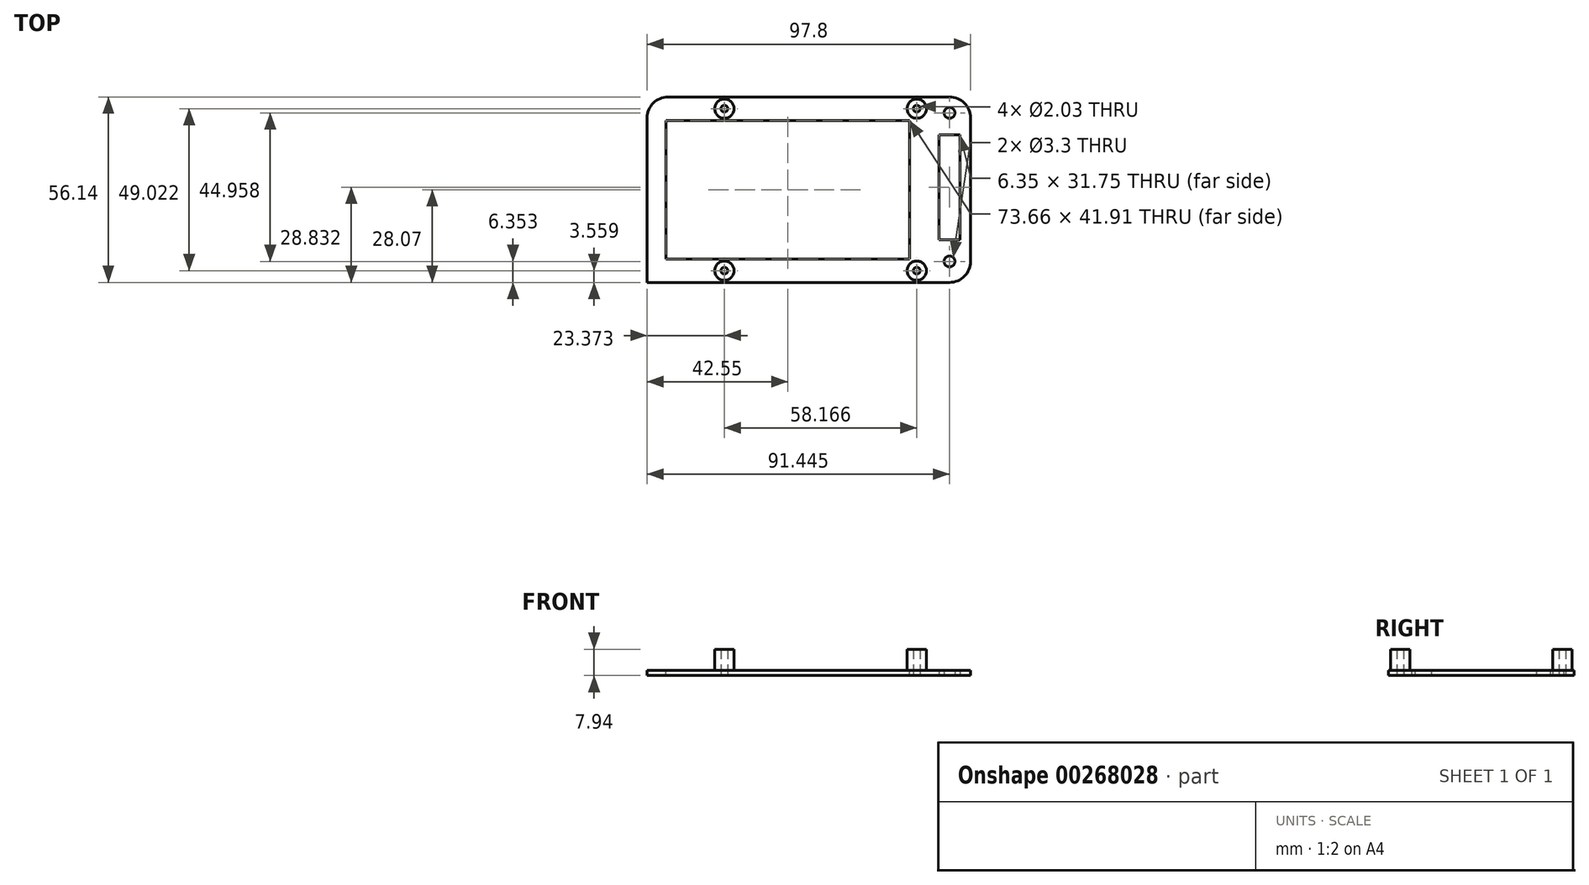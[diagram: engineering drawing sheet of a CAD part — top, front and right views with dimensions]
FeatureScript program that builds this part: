
annotation { "Feature Type Name" : "Feature", "Feature Type Description" : "" }
export const myFeature = defineFeature(function(context is Context, id is Id, definition is map)
    precondition{}
    {
        {
            var Q0;
            Q0=qCreatedBy(makeId("Top.planeOp"),FACE);
            var sketch = newSketch(context, id + "F0", { "sketchPlane" : qUnion([Q0])});
            skLineSegment(sketch, "E0.bottom", {"start": v(42.55, 28.07) * mm, "end": v(-36.2, 28.07) * mm});
            skLineSegment(sketch, "E0.top", {"start": v(42.55, -28.07) * mm, "end": v(-42.55, -28.07) * mm});
            skLineSegment(sketch, "E0.left", {"start": v(42.55, 28.07) * mm, "end": v(42.55, -28.07) * mm});
            skLineSegment(sketch, "E0.right", {"start": v(-42.55, 21.72) * mm, "end": v(-42.55, -28.07) * mm});
            skPoint(sketch, "E0.middle", {"position": v(0, 0) * mm});
            skLineSegment(sketch, "E1.bottom", {"start": v(42.55, 28.07) * mm, "end": v(48.9, 28.07) * mm});
            skLineSegment(sketch, "E1.top", {"start": v(42.55, -28.07) * mm, "end": v(48.9, -28.07) * mm});
            skLineSegment(sketch, "E1.right", {"start": v(55.25, 21.72) * mm, "end": v(55.25, -21.72) * mm});
            skLineSegment(sketch, "E2.bottom", {"start": v(42.55, -28.07) * mm, "end": v(48.9, -28.07) * mm, "construction": true});
            skLineSegment(sketch, "E2.top", {"start": v(42.55, -21.72) * mm, "end": v(48.9, -21.72) * mm, "construction": true});
            skLineSegment(sketch, "E2.left", {"start": v(42.55, -28.07) * mm, "end": v(42.55, -21.72) * mm, "construction": true});
            skLineSegment(sketch, "E2.right", {"start": v(48.9, -28.07) * mm, "end": v(48.9, -21.72) * mm, "construction": true});
            skCircle(sketch, "E3", {"center": v(48.9, -21.72) * mm, "radius": 1.65 * mm});
            skLineSegment(sketch, "E4", {"start": v(48.9, -21.72) * mm, "end": v(48.9, 23.24) * mm, "construction": true});
            skCircle(sketch, "E5", {"center": v(48.9, 23.24) * mm, "radius": 1.65 * mm});
            skLineSegment(sketch, "E6.bottom", {"start": v(-42.55, -28.07) * mm, "end": v(-29.84, -28.07) * mm});
            skLineSegment(sketch, "E6.top", {"start": v(-36.2, -40.77) * mm, "end": v(-36.2, -40.77) * mm});
            skLineSegment(sketch, "E6.left", {"start": v(-42.55, -28.07) * mm, "end": v(-42.55, -34.42) * mm});
            skLineSegment(sketch, "E6.right", {"start": v(-29.84, -28.07) * mm, "end": v(-29.84, -34.42) * mm});
            skLineSegment(sketch, "E7", {"start": v(-42.55, -28.07) * mm, "end": v(-29.84, -40.77) * mm, "construction": true});
            skCircle(sketch, "E8", {"center": v(-36.2, -34.42) * mm, "radius": 1.9 * mm});
            skPoint(sketch, "E9.visualSharp", {"position": v(-29.84, -40.77) * mm});
            skArc(sketch, "E9.filletArc", {"start": v(-36.2, -40.77) * mm, "mid": v(-31.7, -38.9) * mm, "end": v(-29.84, -34.42) * mm});
            skPoint(sketch, "E10.visualSharp", {"position": v(-42.55, -40.77) * mm});
            skArc(sketch, "E10.filletArc", {"start": v(-42.55, -34.42) * mm, "mid": v(-40.69, -38.9) * mm, "end": v(-36.2, -40.77) * mm});
            skPoint(sketch, "E11.visualSharp", {"position": v(55.25, -28.07) * mm});
            skArc(sketch, "E11.filletArc", {"start": v(48.9, -28.07) * mm, "mid": v(53.39, -26.2) * mm, "end": v(55.25, -21.72) * mm});
            skPoint(sketch, "E12.visualSharp", {"position": v(55.25, 28.07) * mm});
            skArc(sketch, "E12.filletArc", {"start": v(55.25, 21.72) * mm, "mid": v(53.39, 26.2) * mm, "end": v(48.9, 28.07) * mm});
            skPoint(sketch, "E13.visualSharp", {"position": v(-42.55, 28.07) * mm});
            skArc(sketch, "E13.filletArc", {"start": v(-36.2, 28.07) * mm, "mid": v(-40.69, 26.2) * mm, "end": v(-42.55, 21.72) * mm});
            skLineSegment(sketch, "E14.bottom", {"start": v(52.07, -15.11) * mm, "end": v(45.72, -15.11) * mm});
            skLineSegment(sketch, "E14.top", {"start": v(52.07, 16.64) * mm, "end": v(45.72, 16.64) * mm});
            skLineSegment(sketch, "E14.left", {"start": v(52.07, -15.11) * mm, "end": v(52.07, 16.64) * mm});
            skLineSegment(sketch, "E14.right", {"start": v(45.72, -15.11) * mm, "end": v(45.72, 16.64) * mm});
            skPoint(sketch, "E14.middle", {"position": v(48.9, 0.76) * mm});
            skSolve(sketch);
        }
        {
            var Q0;
            Q0=makeQuery(id+"F0.imprint","IMPRINT",FACE,{"disambiguationData":[TD([[makeQuery(id+"F0.imprint","IMPRINT",EDGE,{"derivedFrom":sQuery(id+"F0.wireOp",EDGE,"E0.bottom")}),1.0]])]});
            var Q1;
            Q1=makeQuery(id+"F0.imprint","IMPRINT",FACE,{"disambiguationData":[TD([[makeQuery(id+"F0.imprint","IMPRINT",EDGE,{"derivedFrom":sQuery(id+"F0.wireOp",EDGE,"E1.bottom")}),-1.0]])]});
            var Q2;
            Q2=makeQuery(id+"F0.imprint","IMPRINT",FACE,{"disambiguationData":[TD([[makeQuery(id+"F0.imprint","IMPRINT",EDGE,{"derivedFrom":sQuery(id+"F0.wireOp",EDGE,"E6.bottom")}),-1.0]])]});
            extrude(context, id + "F1", {"entities" : qUnion([Q0, Q1, Q2]), "depth" : 1.59 * mm});
        }
        {
            var Q0;
            Q0=makeQuery(id+"F1.opExtrude","CAP_FACE",FACE,{"disambiguationData":[OSD([sQuery(id+"F0.wireOp",EDGE,"E0.bottom"),sQuery(id+"F0.wireOp",EDGE,"E0.top"),sQuery(id+"F0.wireOp",EDGE,"E0.left"),sQuery(id+"F0.wireOp",EDGE,"E0.right")])],"isStart":false});
            var sketch = newSketch(context, id + "F2", { "sketchPlane" : qUnion([Q0])});
            skLineSegment(sketch, "E15.bottom", {"start": v(36.83, -20.96) * mm, "end": v(-36.83, -20.96) * mm});
            skLineSegment(sketch, "E15.top", {"start": v(36.83, 20.96) * mm, "end": v(-36.83, 20.96) * mm});
            skLineSegment(sketch, "E15.left", {"start": v(36.83, -20.96) * mm, "end": v(36.83, 20.96) * mm});
            skLineSegment(sketch, "E15.right", {"start": v(-36.83, -20.96) * mm, "end": v(-36.83, 20.95) * mm});
            skPoint(sketch, "E15.middle", {"position": v(0, 0) * mm});
            skLineSegment(sketch, "E16.bottom", {"start": v(-22.86, 20.96) * mm, "end": v(-16.51, 20.96) * mm});
            skLineSegment(sketch, "E16.top", {"start": v(-22.86, -20.96) * mm, "end": v(-16.51, -20.96) * mm});
            skLineSegment(sketch, "E16.left", {"start": v(-22.86, 20.95) * mm, "end": v(-22.86, -20.96) * mm});
            skLineSegment(sketch, "E16.right", {"start": v(-16.51, 20.95) * mm, "end": v(-16.51, -20.96) * mm});
            skLineSegment(sketch, "E17.bottom", {"start": v(-2.54, 20.96) * mm, "end": v(3.81, 20.96) * mm});
            skLineSegment(sketch, "E17.top", {"start": v(-2.54, -20.96) * mm, "end": v(3.81, -20.96) * mm});
            skLineSegment(sketch, "E17.left", {"start": v(-2.54, 20.95) * mm, "end": v(-2.54, -20.96) * mm});
            skLineSegment(sketch, "E17.right", {"start": v(3.81, 20.95) * mm, "end": v(3.81, -20.96) * mm});
            skLineSegment(sketch, "E18.bottom", {"start": v(17.78, 20.96) * mm, "end": v(24.13, 20.96) * mm});
            skLineSegment(sketch, "E18.top", {"start": v(17.78, -20.96) * mm, "end": v(24.13, -20.96) * mm});
            skLineSegment(sketch, "E18.left", {"start": v(17.78, 20.95) * mm, "end": v(17.78, -20.96) * mm});
            skLineSegment(sketch, "E18.right", {"start": v(24.13, 20.95) * mm, "end": v(24.13, -20.96) * mm});
            skLineSegment(sketch, "E19", {"start": v(-36.83, 14.23) * mm, "end": v(-22.86, 14.23) * mm, "construction": true});
            skLineSegment(sketch, "E20", {"start": v(-2.54, 13.6) * mm, "end": v(-16.51, 13.6) * mm, "construction": true});
            skLineSegment(sketch, "E21", {"start": v(3.81, 12.17) * mm, "end": v(17.78, 12.17) * mm, "construction": true});
            skSolve(sketch);
        }
        {
            var Q0;
            Q0=makeQuery(id+"F2.imprint","IMPRINT",FACE,{"disambiguationData":[TD([[makeQuery(id+"F2.imprint","IMPRINT",EDGE,{"derivedFrom":sQuery(id+"F2.wireOp",EDGE,"E15.bottom")}),-1.0]])]});
            extrude(context, id + "F3", {"entities" : qUnion([Q0]), "operationType" : NewBodyOperationType.REMOVE, "oppositeDirection" : true, "depth" : 6.35 * mm});
        }
        {
            var Q0;
            Q0=makeQuery(id+"F1.opExtrude","CAP_FACE",FACE,{"disambiguationData":[OSD([sQuery(id+"F0.wireOp",EDGE,"E0.bottom"),sQuery(id+"F0.wireOp",EDGE,"E0.top"),sQuery(id+"F0.wireOp",EDGE,"E0.left"),sQuery(id+"F0.wireOp",EDGE,"E0.right")])],"isStart":false});
            var sketch = newSketch(context, id + "F4", { "sketchPlane" : qUnion([Q0])});
            skLineSegment(sketch, "E22.bottom", {"start": v(38.99, -24.51) * mm, "end": v(42.55, -24.51) * mm, "construction": true});
            skLineSegment(sketch, "E22.top", {"start": v(38.99, -28.07) * mm, "end": v(42.55, -28.07) * mm, "construction": true});
            skLineSegment(sketch, "E22.left", {"start": v(38.99, -24.51) * mm, "end": v(38.99, -28.07) * mm, "construction": true});
            skLineSegment(sketch, "E22.right", {"start": v(42.55, -24.51) * mm, "end": v(42.55, -28.07) * mm, "construction": true});
            skCircle(sketch, "E23", {"center": v(38.99, -24.51) * mm, "radius": 1.02 * mm});
            skCircle(sketch, "E24", {"center": v(38.99, -24.51) * mm, "radius": 2.92 * mm});
            skLineSegment(sketch, "E25.bottom", {"start": v(38.99, -24.51) * mm, "end": v(-19.18, -24.51) * mm, "construction": true});
            skLineSegment(sketch, "E25.top", {"start": v(38.99, 24.51) * mm, "end": v(-19.18, 24.51) * mm, "construction": true});
            skLineSegment(sketch, "E25.left", {"start": v(38.99, -24.51) * mm, "end": v(38.99, 24.51) * mm, "construction": true});
            skLineSegment(sketch, "E25.right", {"start": v(-19.18, -24.51) * mm, "end": v(-19.18, 24.51) * mm, "construction": true});
            skCircle(sketch, "E26", {"center": v(-19.18, 24.51) * mm, "radius": 1.02 * mm});
            skCircle(sketch, "E27", {"center": v(-19.18, 24.51) * mm, "radius": 2.92 * mm});
            skCircle(sketch, "E28", {"center": v(38.99, 24.51) * mm, "radius": 1.02 * mm});
            skCircle(sketch, "E29", {"center": v(38.99, 24.51) * mm, "radius": 2.92 * mm});
            skCircle(sketch, "E30", {"center": v(-19.18, -24.51) * mm, "radius": 1.02 * mm});
            skCircle(sketch, "E31", {"center": v(-19.18, -24.51) * mm, "radius": 2.92 * mm});
            skLineSegment(sketch, "E32.bottom", {"start": v(42.55, -28.07) * mm, "end": v(-42.55, -28.07) * mm, "construction": true});
            skLineSegment(sketch, "E32.top", {"start": v(42.55, 28.07) * mm, "end": v(-42.55, 28.07) * mm, "construction": true});
            skLineSegment(sketch, "E32.left", {"start": v(42.55, -28.07) * mm, "end": v(42.55, 28.07) * mm, "construction": true});
            skLineSegment(sketch, "E32.right", {"start": v(-42.55, -28.07) * mm, "end": v(-42.55, 28.07) * mm, "construction": true});
            skSolve(sketch);
        }
        {
            var Q0;
            Q0=makeQuery(id+"F4.imprint","IMPRINT",FACE,{"disambiguationData":[TD([[makeQuery(id+"F4.imprint","IMPRINT",EDGE,{"derivedFrom":sQuery(id+"F4.wireOp",EDGE,"E28")}),-1.0]])]});
            var Q1;
            Q1=makeQuery(id+"F4.imprint","IMPRINT",FACE,{"disambiguationData":[TD([[makeQuery(id+"F4.imprint","IMPRINT",EDGE,{"derivedFrom":sQuery(id+"F4.wireOp",EDGE,"E23")}),-1.0]])]});
            var Q2;
            Q2=makeQuery(id+"F4.imprint","IMPRINT",FACE,{"disambiguationData":[TD([[makeQuery(id+"F4.imprint","IMPRINT",EDGE,{"derivedFrom":sQuery(id+"F4.wireOp",EDGE,"E26")}),-1.0]])]});
            var Q3;
            Q3=makeQuery(id+"F4.imprint","IMPRINT",FACE,{"disambiguationData":[TD([[makeQuery(id+"F4.imprint","IMPRINT",EDGE,{"derivedFrom":sQuery(id+"F4.wireOp",EDGE,"E30")}),-1.0]])]});
            extrude(context, id + "F5", {"entities" : qUnion([Q0, Q1, Q2, Q3]), "operationType" : NewBodyOperationType.ADD, "depth" : 6.35 * mm});
        }
        {
            var Q0;
            Q0=makeQuery(id+"F4.imprint","IMPRINT",FACE,{"disambiguationData":[TD([[makeQuery(id+"F4.imprint","IMPRINT",EDGE,{"derivedFrom":sQuery(id+"F4.wireOp",EDGE,"E23")}),1.0]])]});
            var Q1;
            Q1=makeQuery(id+"F4.imprint","IMPRINT",FACE,{"disambiguationData":[TD([[makeQuery(id+"F4.imprint","IMPRINT",EDGE,{"derivedFrom":sQuery(id+"F4.wireOp",EDGE,"E26")}),1.0]])]});
            var Q2;
            Q2=makeQuery(id+"F4.imprint","IMPRINT",FACE,{"disambiguationData":[TD([[makeQuery(id+"F4.imprint","IMPRINT",EDGE,{"derivedFrom":sQuery(id+"F4.wireOp",EDGE,"E28")}),1.0]])]});
            var Q3;
            Q3=makeQuery(id+"F4.imprint","IMPRINT",FACE,{"disambiguationData":[TD([[makeQuery(id+"F4.imprint","IMPRINT",EDGE,{"derivedFrom":sQuery(id+"F4.wireOp",EDGE,"E30")}),1.0]])]});
            extrude(context, id + "F6", {"entities" : qUnion([Q0, Q1, Q2, Q3]), "operationType" : NewBodyOperationType.REMOVE, "oppositeDirection" : true, "depth" : 6.35 * mm});
        }
    });
